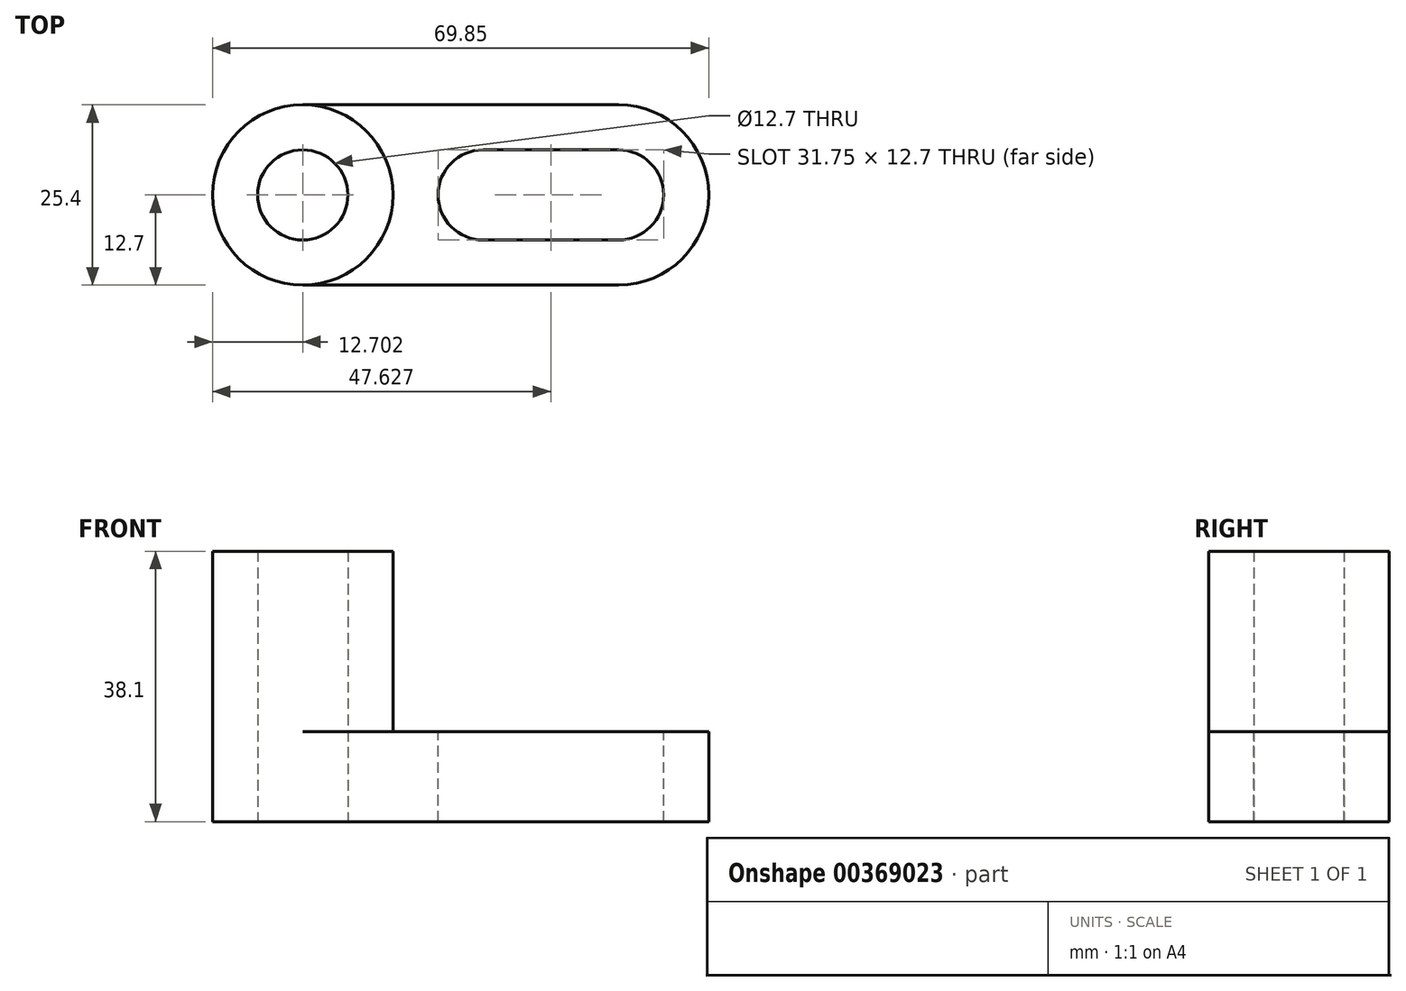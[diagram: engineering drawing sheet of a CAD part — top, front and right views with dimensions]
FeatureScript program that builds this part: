
annotation { "Feature Type Name" : "Feature", "Feature Type Description" : "" }
export const myFeature = defineFeature(function(context is Context, id is Id, definition is map)
    precondition{}
    {
        {
            var Q0;
            Q0=qCreatedBy(makeId("Top.planeOp"),FACE);
            var sketch = newSketch(context, id + "F0", { "sketchPlane" : qUnion([Q0])});
            skLineSegment(sketch, "E0", {"start": v(-42.7, 0) * mm, "end": v(-42.7, 25.4) * mm});
            skLineSegment(sketch, "E1", {"start": v(-42.7, 25.4) * mm, "end": v(27.14, 25.4) * mm});
            skLineSegment(sketch, "E2", {"start": v(27.14, 25.4) * mm, "end": v(27.14, 0) * mm});
            skLineSegment(sketch, "E3", {"start": v(27.14, 0) * mm, "end": v(-42.7, 0) * mm});
            skCircle(sketch, "E4", {"center": v(-30, 12.7) * mm, "radius": 6.35 * mm});
            skPoint(sketch, "E4.centerSnap0", {"position": v(-42.7, 12.7) * mm});
            skCircle(sketch, "E5", {"center": v(-30, 12.7) * mm, "radius": 12.7 * mm});
            skSolve(sketch);
        }
        {
            var Q0;
            {var subQ0=sQuery(id+"F0.wireOp",EDGE,"E1");var subQ1=sQuery(id+"F0.wireOp",EDGE,"E0");var subQ2=makeQuery(id+"F0.imprint","INTERSECT",VERTEX,{"derivedFrom":[subQ1,subQ0]});Q0=makeQuery(id+"F0.imprint","IMPRINT",FACE,{"disambiguationData":[TD([[makeQuery(id+"F0.imprint","IMPRINT",EDGE,{"disambiguationData":[TD([[subQ2,1.0]])],"derivedFrom":subQ1}),-1.0]])]});}
            var Q1;
            {var subQ0=sQuery(id+"F0.wireOp",EDGE,"E2");Q1=makeQuery(id+"F0.imprint","IMPRINT",FACE,{"disambiguationData":[TD([[makeQuery(id+"F0.imprint","IMPRINT",EDGE,{"derivedFrom":subQ0}),-1.0]])]});}
            var Q2;
            {var subQ0=sQuery(id+"F0.wireOp",EDGE,"E3");var subQ1=sQuery(id+"F0.wireOp",EDGE,"E0");var subQ2=makeQuery(id+"F0.imprint","INTERSECT",VERTEX,{"derivedFrom":[subQ1,subQ0]});Q2=makeQuery(id+"F0.imprint","IMPRINT",FACE,{"disambiguationData":[TD([[makeQuery(id+"F0.imprint","IMPRINT",EDGE,{"disambiguationData":[TD([[subQ2,-1.0]])],"derivedFrom":subQ1}),-1.0]])]});}
            var Q3;
            Q3=makeQuery(id+"F0.imprint","IMPRINT",FACE,{"disambiguationData":[TD([[makeQuery(id+"F0.imprint","IMPRINT",EDGE,{"derivedFrom":sQuery(id+"F0.wireOp",EDGE,"E4")}),-1.0]])]});
            extrude(context, id + "F1", {"entities" : qUnion([Q0, Q1, Q2, Q3]), "depth" : 12.7 * mm});
        }
        {
            var Q0;
            Q0=makeQuery(id+"F0.imprint","IMPRINT",FACE,{"disambiguationData":[TD([[makeQuery(id+"F0.imprint","IMPRINT",EDGE,{"derivedFrom":sQuery(id+"F0.wireOp",EDGE,"E4")}),-1.0]])]});
            extrude(context, id + "F2", {"entities" : qUnion([Q0]), "operationType" : NewBodyOperationType.ADD, "depth" : 38.1 * mm});
        }
        {
            var Q0;
            {var subQ0=sQuery(id+"F0.wireOp",EDGE,"E0");var subQ1=sQuery(id+"F0.wireOp",EDGE,"E1");var subQ2=makeQuery(id+"F1.opExtrude","CAP_FACE",FACE,{"disambiguationData":[OSD([subQ0,subQ1,sQuery(id+"F0.wireOp",EDGE,"E2"),sQuery(id+"F0.wireOp",EDGE,"E3"),sQuery(id+"F0.wireOp",EDGE,"E4")])],"isStart":false});Q0=makeQuery(id+"F2.boolean.opBoolean","SPLIT",FACE,{"disambiguationData":[TD([makeQuery(id+"F1.opExtrude","SWEPT_FACE",FACE,{"disambiguationData":[OSD([subQ0])]}),subQ2,makeQuery(id+"F1.opExtrude","SWEPT_FACE",FACE,{"disambiguationData":[OSD([subQ1])]}),makeQuery(id+"F2.opExtrude","SWEPT_FACE",FACE,{"disambiguationData":[OSD([sQuery(id+"F0.wireOp",EDGE,"E5")])]})])],"derivedFrom":subQ2});}
            var Q1;
            {var subQ0=sQuery(id+"F0.wireOp",EDGE,"E0");var subQ1=sQuery(id+"F0.wireOp",EDGE,"E3");var subQ2=makeQuery(id+"F1.opExtrude","CAP_FACE",FACE,{"disambiguationData":[OSD([subQ0,sQuery(id+"F0.wireOp",EDGE,"E1"),sQuery(id+"F0.wireOp",EDGE,"E2"),subQ1,sQuery(id+"F0.wireOp",EDGE,"E4")])],"isStart":false});Q1=makeQuery(id+"F2.boolean.opBoolean","SPLIT",FACE,{"disambiguationData":[TD([makeQuery(id+"F1.opExtrude","SWEPT_FACE",FACE,{"disambiguationData":[OSD([subQ0])]}),subQ2,makeQuery(id+"F1.opExtrude","SWEPT_FACE",FACE,{"disambiguationData":[OSD([subQ1])]}),makeQuery(id+"F2.opExtrude","SWEPT_FACE",FACE,{"disambiguationData":[OSD([sQuery(id+"F0.wireOp",EDGE,"E5")])]})])],"derivedFrom":subQ2});}
            extrude(context, id + "F3", {"entities" : qUnion([Q0, Q1]), "operationType" : NewBodyOperationType.REMOVE, "oppositeDirection" : true, "depth" : 25.4 * mm});
        }
        {
            var Q0;
            {var subQ0=sQuery(id+"F0.wireOp",EDGE,"E3");var subQ1=sQuery(id+"F0.wireOp",EDGE,"E2");var subQ2=sQuery(id+"F0.wireOp",EDGE,"E1");var subQ3=makeQuery(id+"F1.opExtrude","CAP_FACE",FACE,{"disambiguationData":[OSD([sQuery(id+"F0.wireOp",EDGE,"E0"),subQ2,subQ1,subQ0,sQuery(id+"F0.wireOp",EDGE,"E4")])],"isStart":false});Q0=makeQuery(id+"F2.boolean.opBoolean","SPLIT",FACE,{"disambiguationData":[TD([subQ3,makeQuery(id+"F1.opExtrude","SWEPT_FACE",FACE,{"disambiguationData":[OSD([subQ2])]}),makeQuery(id+"F1.opExtrude","SWEPT_FACE",FACE,{"disambiguationData":[OSD([subQ1])]}),makeQuery(id+"F1.opExtrude","SWEPT_FACE",FACE,{"disambiguationData":[OSD([subQ0])]}),makeQuery(id+"F2.opExtrude","SWEPT_FACE",FACE,{"disambiguationData":[OSD([sQuery(id+"F0.wireOp",EDGE,"E5")])]})])],"derivedFrom":subQ3});}
            var sketch = newSketch(context, id + "F4", { "sketchPlane" : qUnion([Q0])});
            skCircle(sketch, "E6", {"center": v(-4.6, 12.7) * mm, "radius": 6.35 * mm});
            skPoint(sketch, "E6.centerSnap0", {"position": v(-17.3, 12.7) * mm});
            skCircle(sketch, "E7", {"center": v(14.44, 12.7) * mm, "radius": 6.35 * mm});
            skLineSegment(sketch, "E8", {"start": v(-4.6, 6.35) * mm, "end": v(14.44, 6.35) * mm});
            skLineSegment(sketch, "E9", {"start": v(14.44, 6.35) * mm, "end": v(14.44, 12.7) * mm});
            skLineSegment(sketch, "E10", {"start": v(14.44, 19.05) * mm, "end": v(-4.6, 19.05) * mm});
            skLineSegment(sketch, "E11", {"start": v(-4.6, 19.05) * mm, "end": v(-4.6, 12.7) * mm});
            skLineSegment(sketch, "E12", {"start": v(-4.6, 6.35) * mm, "end": v(-4.6, 12.7) * mm});
            skLineSegment(sketch, "E13", {"start": v(14.44, 12.7) * mm, "end": v(14.44, 19.05) * mm});
            skSolve(sketch);
        }
        {
            var Q0;
            {var subQ0=sQuery(id+"F4.wireOp",EDGE,"E8");Q0=makeQuery(id+"F4.imprint","IMPRINT",FACE,{"disambiguationData":[TD([[makeQuery(id+"F4.imprint","IMPRINT",EDGE,{"derivedFrom":subQ0}),1.0]])]});}
            var Q1;
            {var subQ2=sQuery(id+"F4.wireOp",EDGE,"E11");Q1=makeQuery(id+"F4.imprint","IMPRINT",FACE,{"disambiguationData":[TD([[makeQuery(id+"F4.imprint","IMPRINT",EDGE,{"derivedFrom":subQ2}),1.0]])]});}
            var Q2;
            {var subQ2=sQuery(id+"F4.wireOp",EDGE,"E11");Q2=makeQuery(id+"F4.imprint","IMPRINT",FACE,{"disambiguationData":[TD([[makeQuery(id+"F4.imprint","IMPRINT",EDGE,{"derivedFrom":subQ2}),-1.0]])]});}
            var Q3;
            {var subQ0=sQuery(id+"F4.wireOp",EDGE,"E9");Q3=makeQuery(id+"F4.imprint","IMPRINT",FACE,{"disambiguationData":[TD([[makeQuery(id+"F4.imprint","IMPRINT",EDGE,{"derivedFrom":subQ0}),1.0]])]});}
            var Q4;
            {var subQ0=sQuery(id+"F4.wireOp",EDGE,"E9");Q4=makeQuery(id+"F4.imprint","IMPRINT",FACE,{"disambiguationData":[TD([[makeQuery(id+"F4.imprint","IMPRINT",EDGE,{"derivedFrom":subQ0}),-1.0]])]});}
            extrude(context, id + "F5", {"entities" : qUnion([Q0, Q1, Q2, Q3, Q4]), "operationType" : NewBodyOperationType.REMOVE, "oppositeDirection" : true, "depth" : 25.4 * mm});
        }
        {
            var Q0;
            {var subQ0=sQuery(id+"F0.wireOp",EDGE,"E3");var subQ1=sQuery(id+"F0.wireOp",EDGE,"E2");var subQ2=sQuery(id+"F0.wireOp",EDGE,"E1");var subQ3=makeQuery(id+"F1.opExtrude","CAP_FACE",FACE,{"disambiguationData":[OSD([sQuery(id+"F0.wireOp",EDGE,"E0"),subQ2,subQ1,subQ0,sQuery(id+"F0.wireOp",EDGE,"E4")])],"isStart":false});Q0=makeQuery(id+"F2.boolean.opBoolean","SPLIT",FACE,{"disambiguationData":[TD([subQ3,makeQuery(id+"F1.opExtrude","SWEPT_FACE",FACE,{"disambiguationData":[OSD([subQ2])]}),makeQuery(id+"F1.opExtrude","SWEPT_FACE",FACE,{"disambiguationData":[OSD([subQ1])]}),makeQuery(id+"F1.opExtrude","SWEPT_FACE",FACE,{"disambiguationData":[OSD([subQ0])]}),makeQuery(id+"F2.opExtrude","SWEPT_FACE",FACE,{"disambiguationData":[OSD([sQuery(id+"F0.wireOp",EDGE,"E5")])]})])],"derivedFrom":subQ3});}
            var sketch = newSketch(context, id + "F6", { "sketchPlane" : qUnion([Q0])});
            skPoint(sketch, "E14", {"position": v(14.44, 25.4) * mm});
            skPoint(sketch, "E15", {"position": v(27.14, 12.7) * mm});
            skPoint(sketch, "E16", {"position": v(14.44, 0) * mm});
            skArc(sketch, "E17", {"start": v(27.14, 12.7) * mm, "mid": v(23.42, 21.68) * mm, "end": v(14.44, 25.4) * mm});
            skArc(sketch, "E18", {"start": v(14.44, 0) * mm, "mid": v(23.42, 3.72) * mm, "end": v(27.14, 12.7) * mm});
            skSolve(sketch);
        }
        {
            var Q0;
            {var subQ0=sQuery(id+"F6.wireOp",EDGE,"E17");Q0=makeQuery(id+"F6.imprint","IMPRINT",FACE,{"disambiguationData":[TD([[makeQuery(id+"F6.imprint","IMPRINT",EDGE,{"derivedFrom":subQ0}),-1.0]])]});}
            var Q1;
            {var subQ0=sQuery(id+"F6.wireOp",EDGE,"E18");Q1=makeQuery(id+"F6.imprint","IMPRINT",FACE,{"disambiguationData":[TD([[makeQuery(id+"F6.imprint","IMPRINT",EDGE,{"derivedFrom":subQ0}),-1.0]])]});}
            extrude(context, id + "F7", {"entities" : qUnion([Q0, Q1]), "operationType" : NewBodyOperationType.REMOVE, "oppositeDirection" : true, "depth" : 25.4 * mm});
        }
    });
